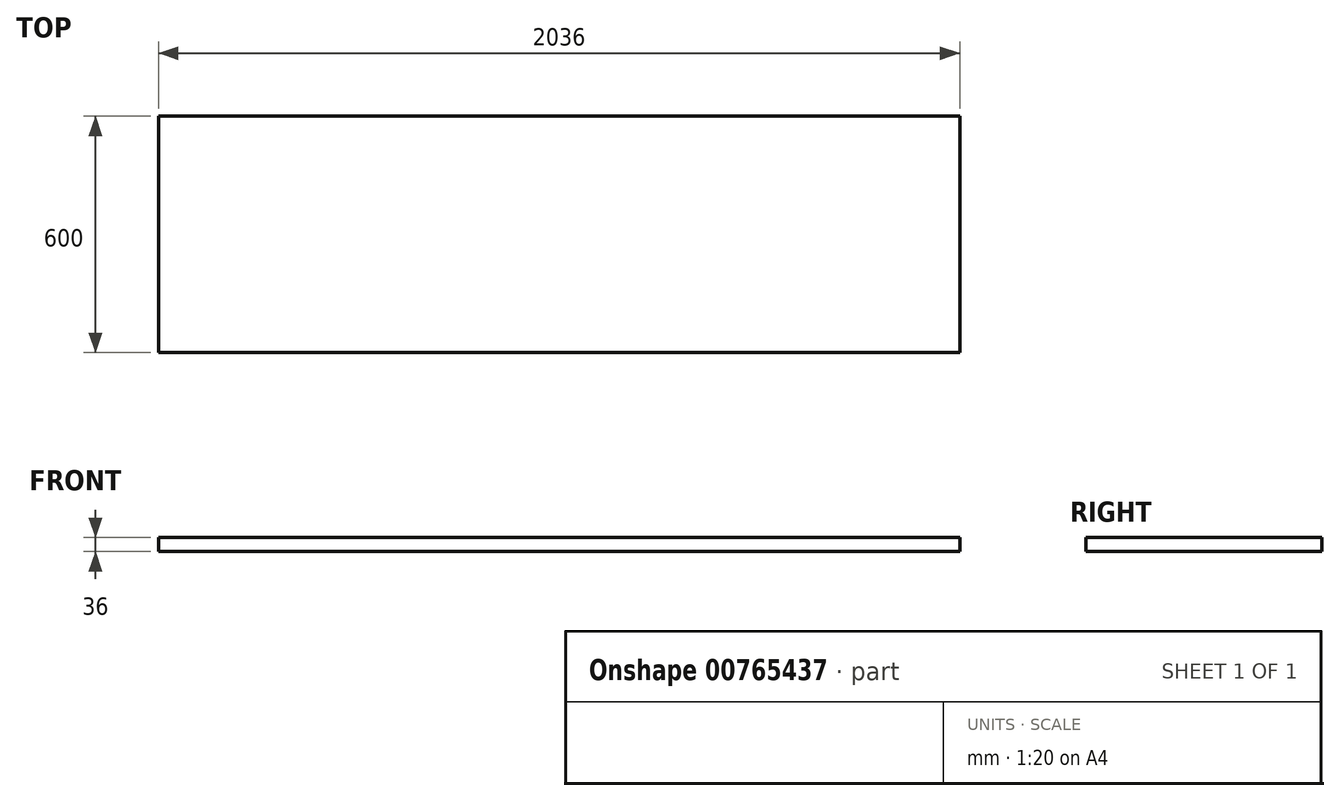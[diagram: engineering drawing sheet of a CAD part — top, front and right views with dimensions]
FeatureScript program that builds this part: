
annotation { "Feature Type Name" : "Feature", "Feature Type Description" : "" }
export const myFeature = defineFeature(function(context is Context, id is Id, definition is map)
    precondition{}
    {
        {
            var Q0;
            Q0=qCreatedBy(makeId("Top.planeOp"),FACE);
            var sketch = newSketch(context, id + "F0", { "sketchPlane" : qUnion([Q0])});
            skLineSegment(sketch, "E0.bottom", {"start": v(-1018, -300) * mm, "end": v(1018, -300) * mm});
            skLineSegment(sketch, "E0.top", {"start": v(-1018, 300) * mm, "end": v(1018, 300) * mm});
            skLineSegment(sketch, "E0.left", {"start": v(-1018, -300) * mm, "end": v(-1018, 300) * mm});
            skLineSegment(sketch, "E0.right", {"start": v(1018, -300) * mm, "end": v(1018, 300) * mm});
            skPoint(sketch, "E0.middle", {"position": v(0, 0) * mm});
            skSolve(sketch);
        }
        {
            var Q0;
            Q0 = qSketchRegion(id + "F0", true);
            extrude(context, id + "F1", {"entities" : qUnion([Q0]), "depth" : 36 * mm, "offsetDistance" : 25 * mm});
        }
    });
